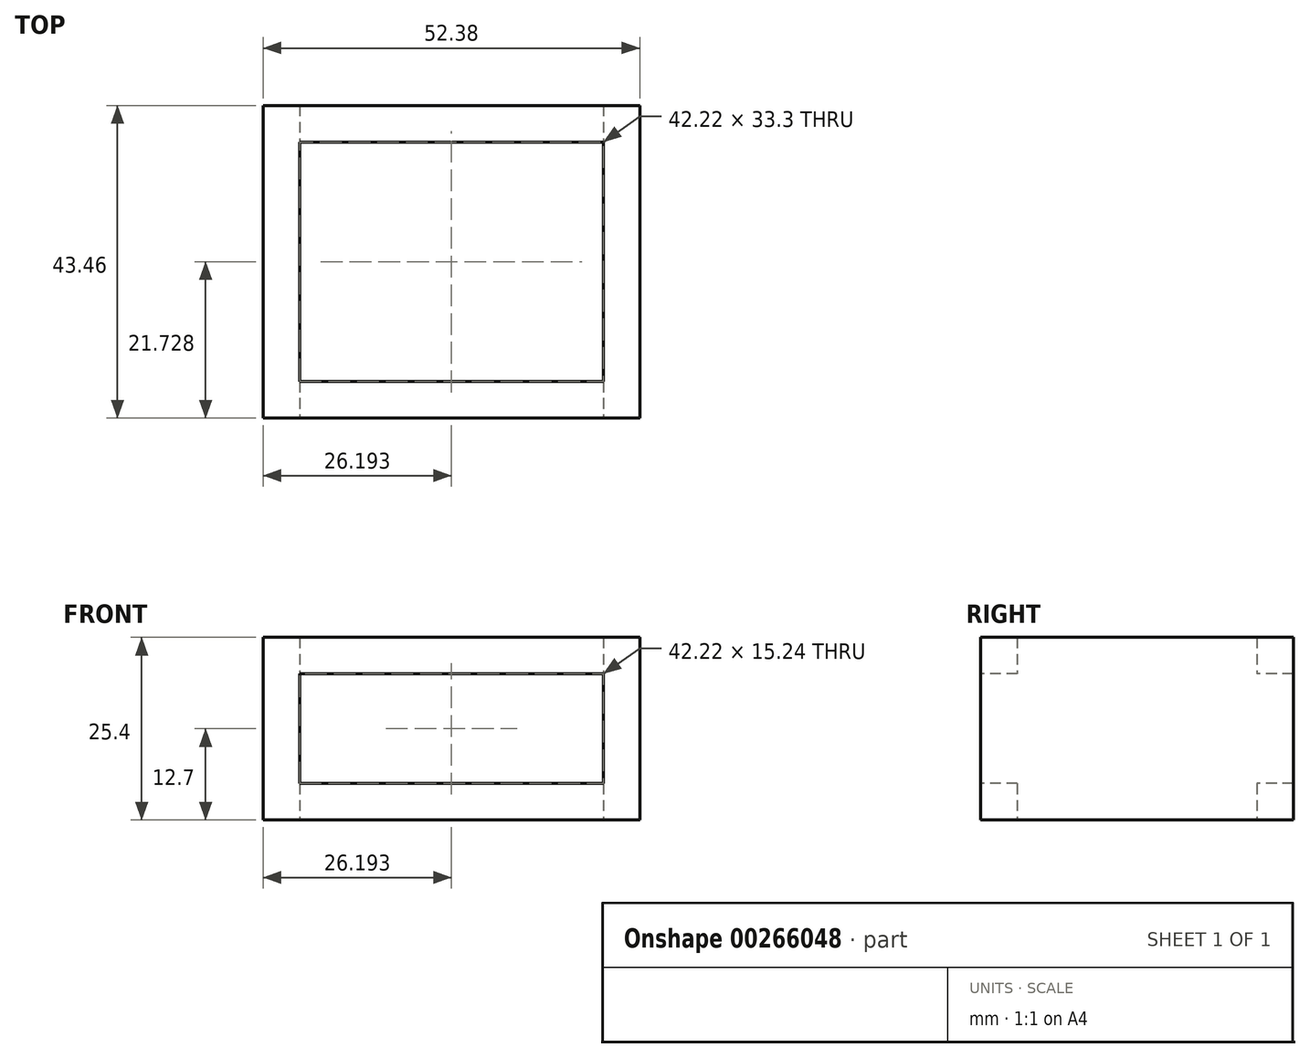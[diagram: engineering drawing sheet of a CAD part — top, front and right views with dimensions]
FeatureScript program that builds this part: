
annotation { "Feature Type Name" : "Feature", "Feature Type Description" : "" }
export const myFeature = defineFeature(function(context is Context, id is Id, definition is map)
    precondition{}
    {
        {
            var Q0;
            Q0=qCreatedBy(makeId("Top.planeOp"),FACE);
            var sketch = newSketch(context, id + "F0", { "sketchPlane" : qUnion([Q0])});
            skLineSegment(sketch, "E0.bottom", {"start": v(-30.5, 39) * mm, "end": v(21.87, 39) * mm});
            skLineSegment(sketch, "E0.top", {"start": v(-30.5, -4.46) * mm, "end": v(21.87, -4.46) * mm});
            skLineSegment(sketch, "E0.left", {"start": v(-30.5, 39) * mm, "end": v(-30.5, -4.46) * mm});
            skLineSegment(sketch, "E0.right", {"start": v(21.87, 39) * mm, "end": v(21.87, -4.46) * mm});
            skSolve(sketch);
        }
        {
            var Q0;
            Q0=makeQuery(id+"F0.imprint","IMPRINT",FACE,{"disambiguationData":[TD([[makeQuery(id+"F0.imprint","IMPRINT",EDGE,{"derivedFrom":sQuery(id+"F0.wireOp",EDGE,"E0.bottom")}),-1.0]])]});
            extrude(context, id + "F1", {"entities" : qUnion([Q0]), "depth" : 25.4 * mm, "offsetDistance" : 25.4 * mm});
        }
        {
            var Q0;
            Q0=makeQuery(id+"F1.opExtrude","CAP_FACE",FACE,{"disambiguationData":[OSD([sQuery(id+"F0.wireOp",EDGE,"E0.bottom"),sQuery(id+"F0.wireOp",EDGE,"E0.top"),sQuery(id+"F0.wireOp",EDGE,"E0.left"),sQuery(id+"F0.wireOp",EDGE,"E0.right")])],"isStart":false});
            var Q1;
            Q1=makeQuery(id+"F1.opExtrude","CAP_FACE",FACE,{"disambiguationData":[OSD([sQuery(id+"F0.wireOp",EDGE,"E0.bottom"),sQuery(id+"F0.wireOp",EDGE,"E0.top"),sQuery(id+"F0.wireOp",EDGE,"E0.left"),sQuery(id+"F0.wireOp",EDGE,"E0.right")])],"isStart":true});
            shell(context, id + "F2", {"entities" : qUnion([Q0, Q1]), "thickness" : 5.08 * mm});
        }
        {
            var Q0;
            Q0=makeQuery(id+"F1.opExtrude","SWEPT_FACE",FACE,{"disambiguationData":[OSD([sQuery(id+"F0.wireOp",EDGE,"E0.top")])]});
            var Q1;
            Q1=makeQuery(id+"F2.opShell","OFFSET_FACE",FACE,{"disambiguationData":[OSD([sQuery(id+"F0.wireOp",EDGE,"E0.top")])]});
            var Q2;
            Q2=makeQuery(id+"F2.opShell","OFFSET_FACE",FACE,{"disambiguationData":[OSD([sQuery(id+"F0.wireOp",EDGE,"E0.bottom")])]});
            var Q3;
            Q3=makeQuery(id+"F1.opExtrude","SWEPT_FACE",FACE,{"disambiguationData":[OSD([sQuery(id+"F0.wireOp",EDGE,"E0.bottom")])]});
            shell(context, id + "F3", {"entities" : qUnion([Q0, Q1, Q2, Q3]), "thickness" : 5.08 * mm});
        }
        {
            var Q0;
            {var subQ0=sQuery(id+"F0.wireOp",EDGE,"E0.left");Q0=makeQuery(id+"F3.opShell","MERGE",FACE,{"derivedFrom":[makeQuery(id+"F1.opExtrude","SWEPT_FACE",FACE,{"disambiguationData":[OSD([subQ0])]}),makeQuery(id+"F2.opShell","OFFSET_FACE",FACE,{"disambiguationData":[OSD([subQ0])]})]});}
            var Q1;
            Q1=makeQuery(id+"F1.opExtrude","SWEPT_FACE",FACE,{"disambiguationData":[OSD([sQuery(id+"F0.wireOp",EDGE,"E0.right")])]});
            var Q2;
            Q2=makeQuery(id+"F1.opExtrude","SWEPT_FACE",FACE,{"disambiguationData":[OSD([sQuery(id+"F0.wireOp",EDGE,"E0.left")])]});
            shell(context, id + "F4", {"entities" : qUnion([Q0, Q1, Q2]), "thickness" : 5.08 * mm});
        }
    });
